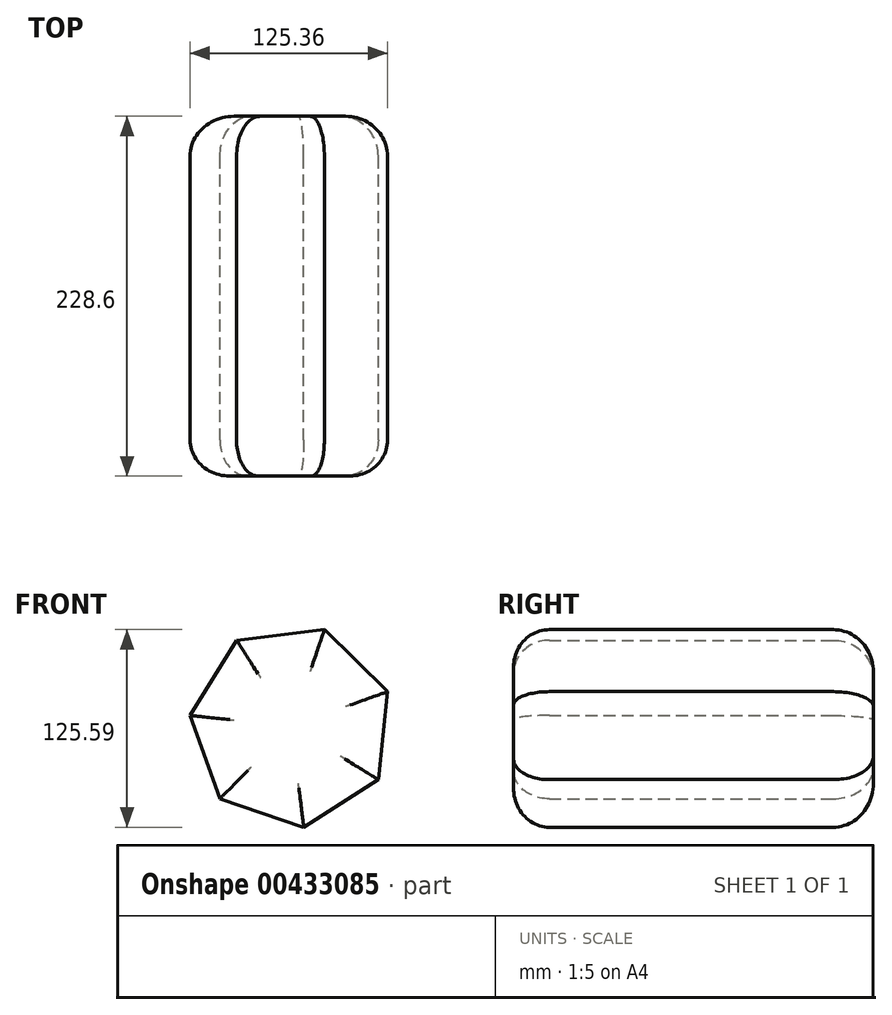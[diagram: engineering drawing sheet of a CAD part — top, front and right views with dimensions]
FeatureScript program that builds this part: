
annotation { "Feature Type Name" : "Feature", "Feature Type Description" : "" }
export const myFeature = defineFeature(function(context is Context, id is Id, definition is map)
    precondition{}
    {
        {
            var Q0;
            Q0=qCreatedBy(makeId("Front.planeOp"),FACE);
            var sketch = newSketch(context, id + "F0", { "sketchPlane" : qUnion([Q0])});
            skCircle(sketch, "E0.cCircle", {"center": v(0, 0) * mm, "radius": 58.35 * mm, "construction": true});
            skLineSegment(sketch, "E0.0", {"start": v(-64.4, 6.73) * mm, "end": v(-34.9, 54.55) * mm});
            skLineSegment(sketch, "E0.1", {"start": v(-34.9, 54.55) * mm, "end": v(20.9, 61.3) * mm});
            skLineSegment(sketch, "E0.2", {"start": v(20.9, 61.3) * mm, "end": v(60.95, 21.88) * mm});
            skLineSegment(sketch, "E0.3", {"start": v(60.95, 21.88) * mm, "end": v(55.1, -34.01) * mm});
            skLineSegment(sketch, "E0.4", {"start": v(55.1, -34.01) * mm, "end": v(7.77, -64.3) * mm});
            skLineSegment(sketch, "E0.5", {"start": v(7.77, -64.3) * mm, "end": v(-45.42, -46.16) * mm});
            skLineSegment(sketch, "E0.6", {"start": v(-45.42, -46.16) * mm, "end": v(-64.4, 6.73) * mm});
            skPoint(sketch, "E0.0.midPoint", {"position": v(-49.65, 30.64) * mm});
            skSolve(sketch);
        }
        {
            var Q0;
            Q0=makeQuery(id+"F0.imprint","IMPRINT",FACE,{"disambiguationData":[TD([[makeQuery(id+"F0.imprint","IMPRINT",EDGE,{"derivedFrom":sQuery(id+"F0.wireOp",EDGE,"E0.0")}),-1.0]])]});
            extrude(context, id + "F1", {"entities" : qUnion([Q0]), "depth" : 228.6 * mm});
        }
        {
            var Q0;
            Q0=makeQuery(id+"F1.opExtrude","CAP_FACE",FACE,{"disambiguationData":[OSD([sQuery(id+"F0.wireOp",EDGE,"E0.0"),sQuery(id+"F0.wireOp",EDGE,"E0.1"),sQuery(id+"F0.wireOp",EDGE,"E0.2"),sQuery(id+"F0.wireOp",EDGE,"E0.3"),sQuery(id+"F0.wireOp",EDGE,"E0.4"),sQuery(id+"F0.wireOp",EDGE,"E0.5"),sQuery(id+"F0.wireOp",EDGE,"E0.6")])],"isStart":false});
            fillet(context, id + "F2", {"entities" : qUnion([Q0]), "radius" : 22.86 * mm, "tangentPropagation" : true, "allowEdgeOverflow" : false});
        }
        {
            var Q0;
            Q0=makeQuery(id+"F1.opExtrude","CAP_FACE",FACE,{"disambiguationData":[OSD([sQuery(id+"F0.wireOp",EDGE,"E0.0"),sQuery(id+"F0.wireOp",EDGE,"E0.1"),sQuery(id+"F0.wireOp",EDGE,"E0.2"),sQuery(id+"F0.wireOp",EDGE,"E0.3"),sQuery(id+"F0.wireOp",EDGE,"E0.4"),sQuery(id+"F0.wireOp",EDGE,"E0.5"),sQuery(id+"F0.wireOp",EDGE,"E0.6")])],"isStart":true});
            fillet(context, id + "F3", {"entities" : qUnion([Q0]), "radius" : 25.4 * mm, "tangentPropagation" : true, "allowEdgeOverflow" : false});
        }
    });
